# Revit family: Beam-Roseburg-RigidLam_LVL
name_source: partatom
category: Structural Framing
units: mm (PartAtom-declared; Revit-internal decimal feet)

## family parameters
Always export as geometry = No
Always vertical = Yes
Classification Number = 23.25.30.11.14.14
Cut with Voids When Loaded = No
Material for Model Behavior = Wood
Section Shape = Not Defined
Shared = No
Show family pre-cut in plan views = Yes
Structural Framing Length Roundoff = 0' - 0"

## types (58) — shared parameters
Application Chart = https://www.roseburg.com
Assembly Code = B10
Building Codes = See PR-L289 & PR-L289C
Construction Details = https://www.arcat.com
EWP Application Chart = https://www.arcat.com
Green Building-LEED = https://www.arcat.com
Installation Guide = https://www.arcat.com
Keynote = 06 40 00
Manufacturer = Roseburg
Material = LVL OSB
Product Data = https://www.arcat.com
Series = RigidLam
Specification = https://www.arcat.com
Structural Material = Engineered Wood - Roseburg - LVL
Testing Data = See ESR1210
URL = https://www.roseburg.com

## per-type parameters (varying)
| type | Description | Model | b | d |
| 1-1/2" x 3-1/2" | RigidLam LVL Beam - 1-1/2" x 3-1/2" | 1-1/2" 3-1/2" | 0' - 1 1/2" | 0' - 3 1/2" |
| 1-1/2" x 4-3/8" | RigidLam LVL Beam - 1-1/2" x 4-3/8" | 1-1/2" 4-3/8" | 0' - 1 1/2" | 0' - 4 3/8" |
| 1-1/2" x 5-1/2" | RigidLam LVL Beam - 1-1/2" x 5-1/2" | 1-1/2" 5-1/2" | 0' - 1 1/2" | 0' - 5 1/2" |
| 1-1/2" x 7-1/4" | RigidLam LVL Beam - 1-1/2" x 7-1/4" | 1-1/2" 7-1/4" | 0' - 1 1/2" | 0' - 7 1/4" |
| 1-1/2" x 9-1/4" | RigidLam LVL Beam - 1-1/2" x 9-1/4" | 1-1/2" 9-1/4" | 0' - 1 1/2" | 0' - 9 1/4" |
| 1-1/2" x 9-1/2" | RigidLam LVL Beam - 1-1/2" x 9-1/2" | 1-1/2" 9-1/2" | 0' - 1 1/2" | 0' - 9 1/2" |
| 1-1/2" x 11-1/4" | RigidLam LVL Beam - 1-1/2" x 11-1/4" | 1-1/2" 11-1/4" | 0' - 1 1/2" | 0' - 11 1/4" |
| 1-1/2" x 11-7/8" | RigidLam LVL Beam - 1-1/2" x 11-7/8" | 1-1/2" 11-7/8" | 0' - 1 1/2" | 0' - 11 7/8" |
| 1-1/2" x 14" | RigidLam LVL Beam - 1-1/2" x 14" | 1-1/2" 14" | 0' - 1 1/2" | 1' - 2" |
| 1-1/2" x 16" | RigidLam LVL Beam - 1-1/2" x 16" | 1-1/2" 16" | 0' - 1 1/2" | 1' - 4" |
| 1-1/2" x 18" | RigidLam LVL Beam - 1-1/2" x 18" | 1-1/2" 18" | 0' - 1 1/2" | 1' - 6" |
| 1-1/2" x 20" | RigidLam LVL Beam - 1-1/2" x 20" | 1-1/2" 20" | 0' - 1 1/2" | 1' - 8" |
| 1-1/2" x 22" | RigidLam LVL Beam - 1-1/2" x 22" | 1-1/2" 22" | 0' - 1 1/2" | 1' - 10" |
| 1-1/2" x 24" | RigidLam LVL Beam - 1-1/2" x 24" | 1-1/2" 24" | 0' - 1 1/2" | 2' - 0" |
| 1-3/4" x 3-1/2" | RigidLam LVL Beam - 1-3/4" x 3-1/2" | 1-3/4" 3-1/2" | 0' - 1 3/4" | 0' - 3 1/2" |
| 1-3/4" x 4-3/8" | RigidLam LVL Beam - 1-3/4" x 4-3/8" | 1-3/4" 4-3/8" | 0' - 1 3/4" | 0' - 4 3/8" |
| 1-3/4" x 5-1/2" | RigidLam LVL Beam - 1-3/4" x 5-1/2" | 1-3/4" 5-1/2" | 0' - 1 3/4" | 0' - 5 1/2" |
| 1-3/4" x 7-1/4" | RigidLam LVL Beam - 1-3/4" x 7-1/4" | 1-3/4" 7-1/4" | 0' - 1 3/4" | 0' - 7 1/4" |
| 1-3/4" x 9-1/4" | RigidLam LVL Beam - 1-3/4" x 9-1/4" | 1-3/4" 9-1/4" | 0' - 1 3/4" | 0' - 9 1/4" |
| 1-3/4" x 9-1/2" | RigidLam LVL Beam - 1-3/4" x 9-1/2" | 1-3/4" 9-1/2" | 0' - 1 3/4" | 0' - 9 1/2" |
| 1-3/4" x 11-1/4" | RigidLam LVL Beam - 1-3/4" x 11-1/4" | 1-3/4" 11-1/4" | 0' - 1 3/4" | 0' - 11 1/4" |
| 1-3/4" x 11-7/8" | RigidLam LVL Beam - 1-3/4" x 11-7/8" | 1-3/4" 11-7/8" | 0' - 1 3/4" | 0' - 11 7/8" |
| 1-3/4" x 14" | RigidLam LVL Beam - 1-3/4" x 14" | 1-3/4" 14" | 0' - 1 3/4" | 1' - 2" |
| 1-3/4" x 16" | RigidLam LVL Beam - 1-3/4" x 16" | 1-3/4" 16" | 0' - 1 3/4" | 1' - 4" |
| 1-3/4" x 18" | RigidLam LVL Beam - 1-3/4" x 18" | 1-3/4" 18" | 0' - 1 3/4" | 1' - 6" |
| 1-3/4" x 20" | RigidLam LVL Beam - 1-3/4" x 20" | 1-3/4" 20" | 0' - 1 3/4" | 1' - 8" |
| 1-3/4" x 22" | RigidLam LVL Beam - 1-3/4" x 22" | 1-3/4" 22" | 0' - 1 3/4" | 1' - 10" |
| 1-3/4" x 24" | RigidLam LVL Beam - 1-3/4" x 24" | 1-3/4" 24" | 0' - 1 3/4" | 2' - 0" |
| 7" x 9-1/2" | RigidLam LVL Beam - 7" x 9-1/2" | 7" 9-1/2" | 0' - 7" | 0' - 9 1/2" |
| 7" x 11-1/4" | RigidLam LVL Beam - 7" x 11-1/4" | 7" 11-1/4" | 0' - 7" | 0' - 11 1/4" |
| 7" x 11-7/8" | RigidLam LVL Beam - 7" x 11-7/8" | 7" 11-7/8" | 0' - 7" | 0' - 11 7/8" |
| 7" x 14" | RigidLam LVL Beam - 7" x 14" | 7" 14" | 0' - 7" | 1' - 2" |
| 7" x 16" | RigidLam LVL Beam - 7" x 16" | 7" 16" | 0' - 7" | 1' - 4" |
| 7" x 18" | RigidLam LVL Beam - 7" x 18" | 7" 18" | 0' - 7" | 1' - 6" |
| 7" x 20" | RigidLam LVL Beam - 7" x 20" | 7" 20" | 0' - 7" | 1' - 8" |
| 7" x 22" | RigidLam LVL Beam - 7" x 22" | 7" 22" | 0' - 7" | 1' - 10" |
| 7" x 24" | RigidLam LVL Beam - 7" x 24" | 7" 24" | 0' - 7" | 2' - 0" |
| 5-1/4" x 9-1/2" | RigidLam LVL Beam - 5-1/4" x 9-1/2" | 5-1/4" 9-1/2" | 0' - 5 1/4" | 0' - 9 1/2" |
| 5-1/4" x 11-1/4" | RigidLam LVL Beam - 5-1/4" x 11-1/4" | 5-1/4" 11-1/4" | 0' - 5 1/4" | 0' - 11 1/4" |
| 5-1/4" x 11-7/8" | RigidLam LVL Beam - 5-1/4" x 11-7/8" | 5-1/4" 11-7/8" | 0' - 5 1/4" | 0' - 11 7/8" |
| 5-1/4" x 14" | RigidLam LVL Beam - 5-1/4" x 14" | 5-1/4" 14" | 0' - 5 1/4" | 1' - 2" |
| 5-1/4" x 16" | RigidLam LVL Beam - 5-1/4" x 16" | 5-1/4" 16" | 0' - 5 1/4" | 1' - 4" |
| 5-1/4" x 18" | RigidLam LVL Beam - 5-1/4" x 18" | 5-1/4" 18" | 0' - 5 1/4" | 1' - 6" |
| 5-1/4" x 20" | RigidLam LVL Beam - 5-1/4" x 20" | 5-1/4" 20" | 0' - 5 1/4" | 1' - 8" |
| 5-1/4" x 22" | RigidLam LVL Beam - 5-1/4" x 22" | 5-1/4" 22" | 0' - 5 1/4" | 1' - 10" |
| 5-1/4" x 24" | RigidLam LVL Beam - 5-1/4" x 24" | 5-1/4" 24" | 0' - 5 1/4" | 2' - 0" |
| 3-1/2" x 5-1/2" | RigidLam LVL Beam - 3-1/2" x 5-1/2" | 3-1/2" 5-1/2" | 0' - 3 1/2" | 0' - 5 1/2" |
| 3-1/2" x 7-1/4" | RigidLam LVL Beam - 3-1/2" x 7-1/4" | 3-1/2" 7-1/4" | 0' - 3 1/2" | 0' - 7 1/4" |
| 3-1/2" x 9-1/4" | RigidLam LVL Beam - 3-1/2" x 9-1/4" | 3-1/2" 9-1/4" | 0' - 3 1/2" | 0' - 9 1/4" |
| 3-1/2" x 9-1/2" | RigidLam LVL Beam - 3-1/2" x 9-1/2" | 3-1/2" 9-1/2" | 0' - 3 1/2" | 0' - 9 1/2" |
| 3-1/2" x 11-1/4" | RigidLam LVL Beam - 3-1/2" x 11-1/4" | 3-1/2" 11-1/4" | 0' - 3 1/2" | 0' - 11 1/4" |
| 3-1/2" x 11-7/8" | RigidLam LVL Beam - 3-1/2" x 11-7/8" | 3-1/2" 11-7/8" | 0' - 3 1/2" | 0' - 11 7/8" |
| 3-1/2" x 14" | RigidLam LVL Beam - 3-1/2" x 14" | 3-1/2" 14" | 0' - 3 1/2" | 1' - 2" |
| 3-1/2" x 16" | RigidLam LVL Beam - 3-1/2" x 16" | 3-1/2" 16" | 0' - 3 1/2" | 1' - 4" |
| 3-1/2" x 18" | RigidLam LVL Beam - 3-1/2" x 18" | 3-1/2" 18" | 0' - 3 1/2" | 1' - 6" |
| 3-1/2" x 20" | RigidLam LVL Beam - 3-1/2" x 20" | 3-1/2" 20" | 0' - 3 1/2" | 1' - 8" |
| 3-1/2" x 22" | RigidLam LVL Beam - 3-1/2" x 22" | 3-1/2" 22" | 0' - 3 1/2" | 1' - 10" |
| 3-1/2" x 24" | RigidLam LVL Beam - 3-1/2" x 24" | 3-1/2" 24" | 0' - 3 1/2" | 2' - 0" |

## geometry (parser evidence)
native form markers: Sweep x1
no freeform markers — native parametric forms only
